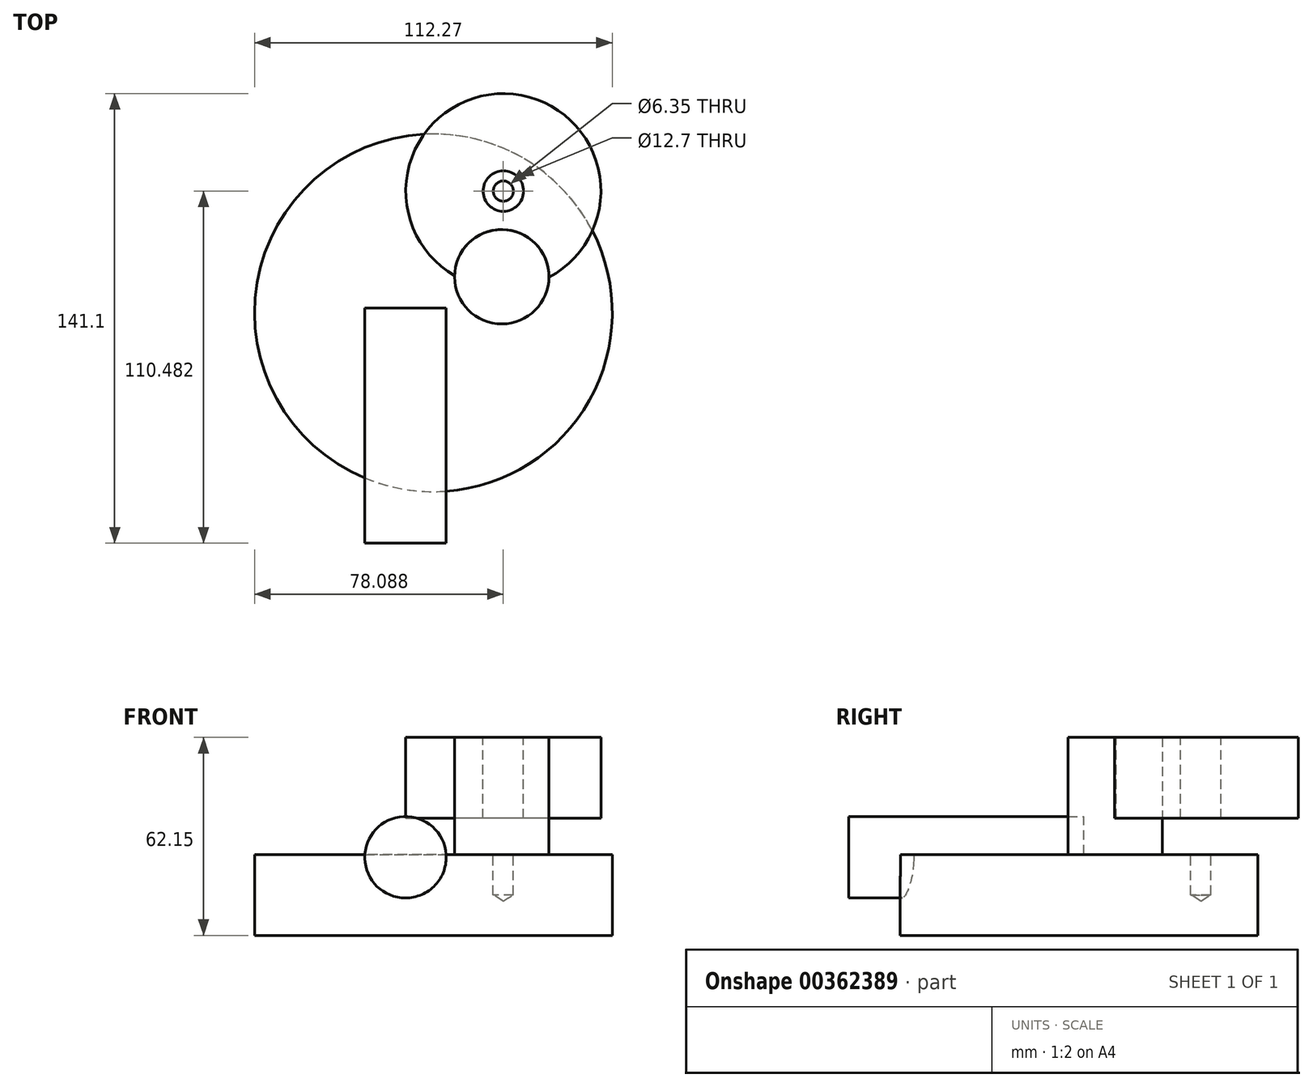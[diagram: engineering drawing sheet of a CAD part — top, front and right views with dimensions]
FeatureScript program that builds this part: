
annotation { "Feature Type Name" : "Feature", "Feature Type Description" : "" }
export const myFeature = defineFeature(function(context is Context, id is Id, definition is map)
    precondition{}
    {
        {
            var Q0;
            Q0=qCreatedBy(makeId("Top.planeOp"),FACE);
            var sketch = newSketch(context, id + "F0", { "sketchPlane" : qUnion([Q0])});
            skCircle(sketch, "E0", {"center": v(0.02, -1.46) * mm, "radius": 56.13 * mm});
            skSolve(sketch);
        }
        {
            var Q0;
            Q0=qCreatedBy(makeId("Top.planeOp"),FACE);
            var sketch = newSketch(context, id + "F1", { "sketchPlane" : qUnion([Q0])});
            skCircle(sketch, "E1", {"center": v(21.47, 9.87) * mm, "radius": 14.81 * mm});
            skSolve(sketch);
        }
        {
            var Q0;
            Q0=makeQuery(id+"F1.imprint","IMPRINT",FACE,{"disambiguationData":[TD([[makeQuery(id+"F1.imprint","IMPRINT",EDGE,{"derivedFrom":sQuery(id+"F1.wireOp",EDGE,"E1")}),1.0]])]});
            extrude(context, id + "F2", {"entities" : qUnion([Q0]), "depth" : 62.15 * mm});
        }
        {
            var Q0;
            Q0=makeQuery(id+"F0.imprint","IMPRINT",FACE,{"disambiguationData":[TD([[makeQuery(id+"F0.imprint","IMPRINT",EDGE,{"derivedFrom":sQuery(id+"F0.wireOp",EDGE,"E0")}),1.0]])]});
            extrude(context, id + "F3", {"entities" : qUnion([Q0]), "operationType" : NewBodyOperationType.ADD, "depth" : 25.4 * mm});
        }
        {
            var Q0;
            Q0=makeQuery(id+"F2.opExtrude","CAP_FACE",FACE,{"disambiguationData":[OSD([sQuery(id+"F1.wireOp",EDGE,"E1")])],"isStart":false});
            var sketch = newSketch(context, id + "F4", { "sketchPlane" : qUnion([Q0])});
            skCircle(sketch, "E2", {"center": v(21.97, 36.74) * mm, "radius": 30.62 * mm});
            skSolve(sketch);
        }
        {
            var Q0;
            {var subQ0=sQuery(id+"F4.wireOp",EDGE,"E2");var subQ1=makeQuery(id+"F2.opExtrude","CAP_EDGE",EDGE,{"disambiguationData":[OSD([sQuery(id+"F1.wireOp",EDGE,"E1")])],"isStart":false});var subQ2=makeQuery(id+"F4.imprint","INTERSECT",VERTEX,{"disambiguationData":[OD(0.0)],"derivedFrom":[subQ1,subQ0]});Q0=makeQuery(id+"F4.imprint","IMPRINT",FACE,{"disambiguationData":[TD([[makeQuery(id+"F4.imprint","IMPRINT",EDGE,{"disambiguationData":[TD([[subQ2,1.0]])],"derivedFrom":subQ0}),1.0]])]});}
            extrude(context, id + "F5", {"entities" : qUnion([Q0]), "oppositeDirection" : true, "depth" : 25.4 * mm});
        }
        {
            var Q0;
            Q0=qCreatedBy(makeId("Front.planeOp"),FACE);
            var sketch = newSketch(context, id + "F6", { "sketchPlane" : qUnion([Q0])});
            skCircle(sketch, "E3", {"center": v(-8.74, 24.52) * mm, "radius": 12.78 * mm});
            skSolve(sketch);
        }
        {
            var Q0;
            Q0=makeQuery(id+"F6.imprint","IMPRINT",FACE,{"disambiguationData":[TD([[makeQuery(id+"F6.imprint","IMPRINT",EDGE,{"derivedFrom":sQuery(id+"F6.wireOp",EDGE,"E3")}),1.0]])]});
            extrude(context, id + "F7", {"entities" : qUnion([Q0]), "operationType" : NewBodyOperationType.ADD, "depth" : 73.74 * mm});
        }
        {
            var Q0;
            Q0=makeQuery(id+"F7.opExtrude","CAP_FACE",FACE,{"disambiguationData":[OSD([sQuery(id+"F6.wireOp",EDGE,"E3")])],"isStart":false});
            var sketch = newSketch(context, id + "F8", { "sketchPlane" : qUnion([Q0])});
            skCircle(sketch, "E4", {"center": v(-8.74, 24.52) * mm, "radius": 6.62 * mm});
            skSolve(sketch);
        }
        {
            var Q0;
            Q0 = qSketchRegion(id + "F8", true);
            extrude(context, id + "F9", {"entities" : qUnion([Q0]), "operationType" : NewBodyOperationType.ADD, "endBound" : BoundingType.UP_TO_NEXT, "oppositeDirection" : true, "depth" : 89.61 * mm});
        }
        {
            var Q0;
            Q0=sQuery(id+"F4.wireOp",VERTEX,"E2.center");
            var Q1;
            Q1=makeQuery(id+"F2.opExtrude","SWEPT_BODY",BODY,{"disambiguationData":[OSD([sQuery(id+"F1.wireOp",EDGE,"E1")])]});
            var Q2;
            Q2=makeQuery(id+"F5.opExtrude","SWEPT_BODY",BODY,{"disambiguationData":[OSD([sQuery(id+"F1.wireOp",EDGE,"E1"),sQuery(id+"F4.wireOp",EDGE,"E2")])]});
            hole(context, id + "F10", {"style" : HoleStyle.SIMPLE, "endStyle" : HoleEndStyle.BLIND_IN_LAST, "holeDiameter" : 12.7 * mm, "tapDrillDiameter" : 6.35 * mm, "majorDiameter" : 6.35 * mm, "holeDepth" : 12.7 * mm, "isTappedThrough" : true, "tappedDepth" : 12.7 * mm, "tapClearance" : 3, "locations" : qUnion([Q0]), "scope" : qUnion([Q1, Q2])});
        }
    });
